# Revit family: DC_Rheem_PLM_HeavyDutyGas_630260
name_source: partatom
category: Plumbing Fixtures
units: mm (PartAtom-declared; Revit-internal decimal feet)

## family parameters
Cut with Voids When Loaded = No
Host = Face
Part Type = Normal
Room Calculation Point = No
Round Connector Dimension = Use Radius
Shared = No

## types (2) — shared parameters
CylinderDiameterD2_ANZRS = 593 mm  [stored 1.94554 ft]
CylinderRadius_ANZRS = 297 mm
GasInletPipeRadius_ANZRS = 10 mm  [stored 0.0328084 ft]
Manufacturer = Rheem
Materials_ANZRS = Rheem - Joey Grey Steel
T&PRValveRadius_ANZRS = 16 mm  [stored 0.0524934 ft]
Thickness_ANZRS = 35 mm
TopDiameterD1_ANZRS = 189 mm
Type Comments = 385L first hour delivery @ 50oC rise
URL = http://www.rheem.com.au
zero-valued in all types: Default Elevation

## per-type parameters (varying)
| type | ColdWaterInletPipeDiameter_ANZRS | ColdWaterInletPipeRadius_ANZRS | Description | HotWaterOutletPipeDiameter_ANZRS | HotWaterOutletPipeRadius_ANZRS | Model |
| Heavy Duty Gas Storage - Outdoor - 260L - 51 MJ/h - Natural gas | 32 mm  [stored 0.104987 ft] | 16 mm  [stored 0.0524934 ft] | Heavy Duty Gas Storage - Outdoor - 260L - 51 MJ/h - Natural gas | 32 mm  [stored 0.104987 ft] | 16 mm  [stored 0.0524934 ft] | 630260N0 |
| Heavy Duty Gas Storage - Outdoor - 260L - 47 MJ/h - Propane gas | 0 mm  [stored 0 ft] | 0 mm  [stored 0 ft] | Heavy Duty Gas Storage - Outdoor - 260L - 47 MJ/h - Propane gas (Propane Gas not avaible in NSW) | 0 mm  [stored 0 ft] | 0 mm  [stored 0 ft] | 630260P0 |

note: [stored X ft] marks values corroborated as IEEE doubles in the binary element streams (Revit-internal decimal feet)

## geometry (parser evidence)
native form markers: Blend x6, Sweep x5
no freeform markers — native parametric forms only
